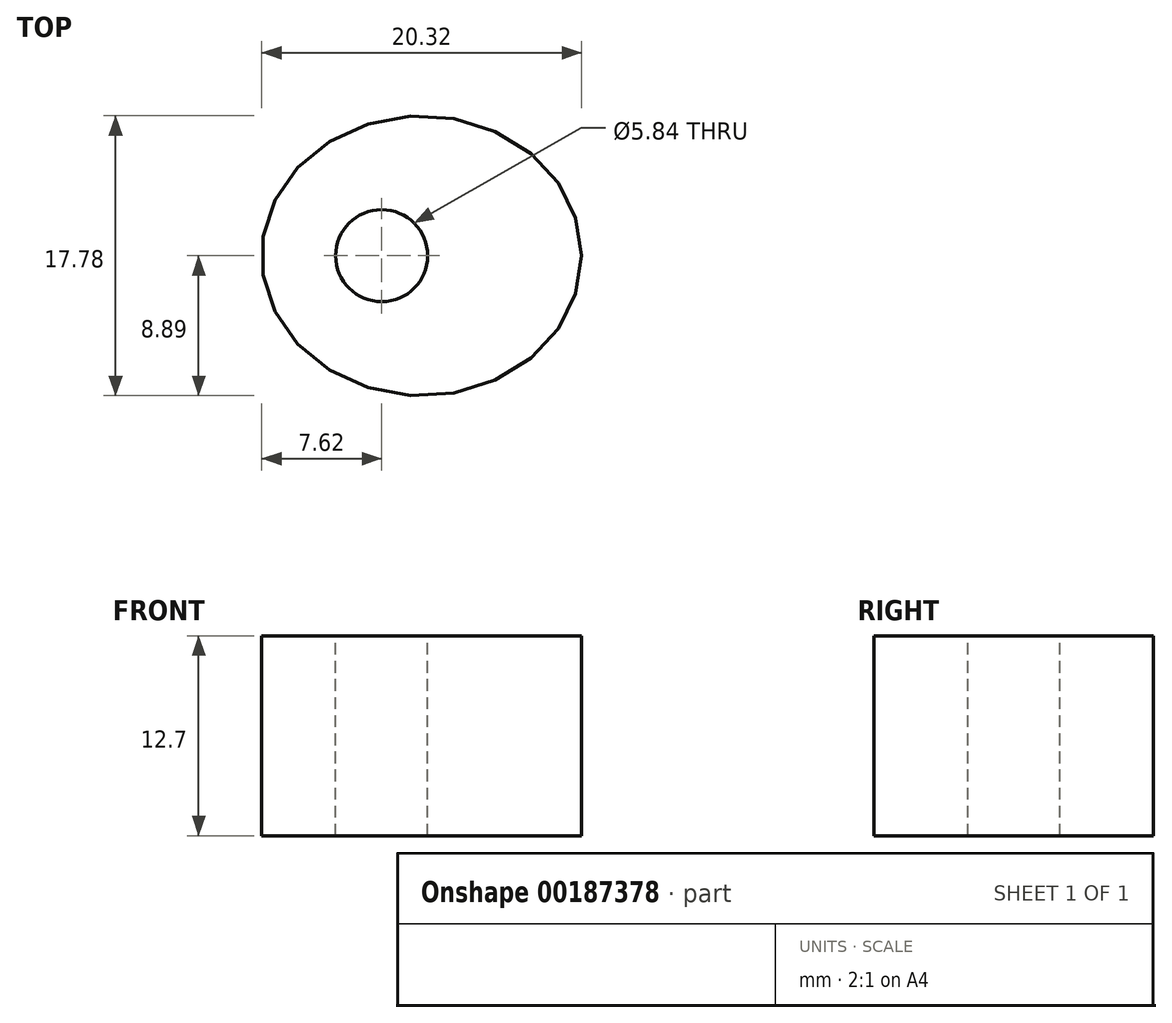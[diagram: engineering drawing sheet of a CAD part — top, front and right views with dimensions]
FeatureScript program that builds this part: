
annotation { "Feature Type Name" : "Feature", "Feature Type Description" : "" }
export const myFeature = defineFeature(function(context is Context, id is Id, definition is map)
    precondition{}
    {
        {
            var Q0;
            Q0=qCreatedBy(makeId("Top.planeOp"),FACE);
            var sketch = newSketch(context, id + "F0", { "sketchPlane" : qUnion([Q0])});
            skEllipse(sketch, "E0", {"center": v(0, 0) * mm, "majorRadius": 10.16 * mm, "minorRadius": 8.9 * mm, "majorAxis": v(1, 0)});
            skCircle(sketch, "E1", {"center": v(-2.54, 0) * mm, "radius": 2.92 * mm});
            skSolve(sketch);
        }
        {
            var Q0;
            Q0=makeQuery(id+"F0.imprint","IMPRINT",FACE,{"disambiguationData":[TD([[makeQuery(id+"F0.imprint","IMPRINT",EDGE,{"derivedFrom":sQuery(id+"F0.wireOp",EDGE,"E0")}),1.0]])]});
            extrude(context, id + "F1", {"entities" : qUnion([Q0]), "oppositeDirection" : true, "depth" : 12.7 * mm});
        }
    });
